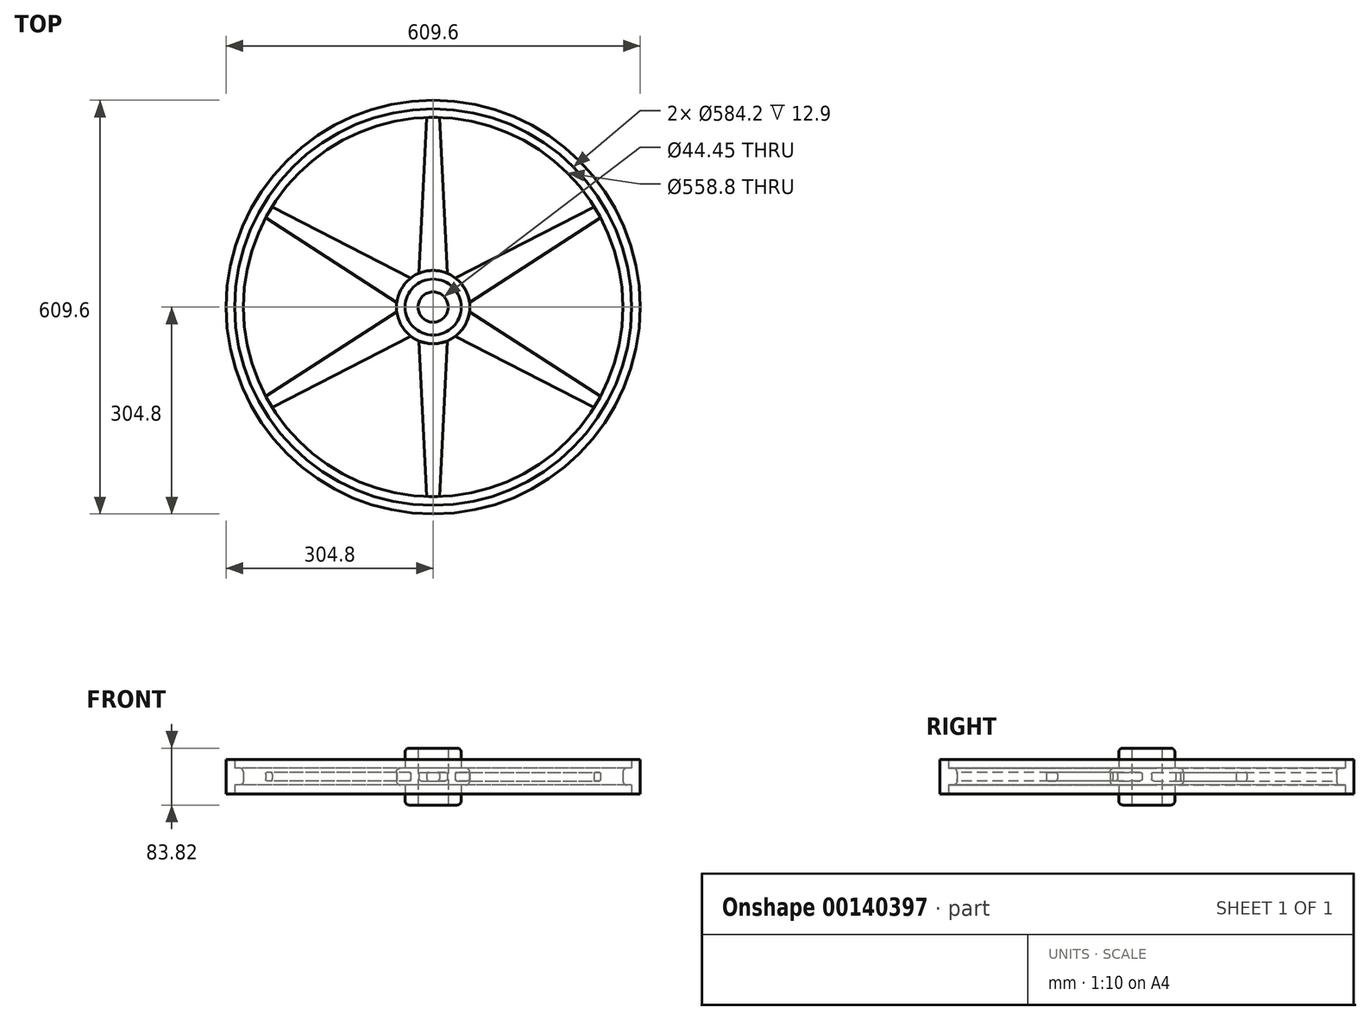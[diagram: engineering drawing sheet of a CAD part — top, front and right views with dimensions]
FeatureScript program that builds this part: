
annotation { "Feature Type Name" : "Feature", "Feature Type Description" : "" }
export const myFeature = defineFeature(function(context is Context, id is Id, definition is map)
    precondition{}
    {
        {
            var Q0;
            Q0=qCreatedBy(makeId("Top.planeOp"),FACE);
            var sketch = newSketch(context, id + "F0", { "sketchPlane" : qUnion([Q0])});
            skCircle(sketch, "E0", {"center": v(0, 0) * mm, "radius": 22.23 * mm});
            skCircle(sketch, "E1.0", {"center": v(0, 0) * mm, "radius": 41.28 * mm});
            skCircle(sketch, "E2.0", {"center": v(0, 0) * mm, "radius": 53.98 * mm});
            skCircle(sketch, "E3", {"center": v(0, 0) * mm, "radius": 304.8 * mm});
            skCircle(sketch, "E4.0", {"center": v(0, 0) * mm, "radius": 292.1 * mm});
            skCircle(sketch, "E5.0", {"center": v(0, 0) * mm, "radius": 279.4 * mm});
            skLineSegment(sketch, "E6", {"start": v(-20.86, 49.78) * mm, "end": v(-9.37, 279.24) * mm});
            skLineSegment(sketch, "E7.MirrorCS", {"start": v(20.86, 49.78) * mm, "end": v(9.37, 279.24) * mm});
            skLineSegment(sketch, "E8.1.0", {"start": v(-53.54, 6.83) * mm, "end": v(-246.52, 131.5) * mm});
            skLineSegment(sketch, "E8.1.1", {"start": v(-32.69, 42.95) * mm, "end": v(-237.15, 147.74) * mm});
            skLineSegment(sketch, "E8.2.0", {"start": v(-32.69, -42.95) * mm, "end": v(-237.15, -147.74) * mm});
            skLineSegment(sketch, "E8.2.1", {"start": v(-53.54, -6.83) * mm, "end": v(-246.52, -131.5) * mm});
            skLineSegment(sketch, "E9.1.3.0", {"start": v(20.86, -49.78) * mm, "end": v(9.37, -279.24) * mm});
            skLineSegment(sketch, "E9.3.3.0", {"start": v(-20.86, -49.78) * mm, "end": v(-9.37, -279.24) * mm});
            skLineSegment(sketch, "E9.1.4.0", {"start": v(53.54, -6.83) * mm, "end": v(246.52, -131.5) * mm});
            skLineSegment(sketch, "E9.3.4.0", {"start": v(32.69, -42.95) * mm, "end": v(237.15, -147.74) * mm});
            skLineSegment(sketch, "E9.1.5.0", {"start": v(32.69, 42.95) * mm, "end": v(237.15, 147.74) * mm});
            skLineSegment(sketch, "E9.3.5.0", {"start": v(53.54, 6.83) * mm, "end": v(246.52, 131.5) * mm});
            skSolve(sketch);
        }
        {
            var Q0;
            Q0=makeQuery(id+"F0.imprint","IMPRINT",FACE,{"disambiguationData":[TD([[makeQuery(id+"F0.imprint","IMPRINT",EDGE,{"derivedFrom":sQuery(id+"F0.wireOp",EDGE,"E4.0")}),1.0]])]});
            var Q1;
            Q1=makeQuery(id+"F0.imprint","IMPRINT",FACE,{"disambiguationData":[TD([[makeQuery(id+"F0.imprint","IMPRINT",EDGE,{"derivedFrom":sQuery(id+"F0.wireOp",EDGE,"E1.0")}),-1.0]])]});
            extrude(context, id + "F1", {"entities" : qUnion([Q0, Q1]), "endBound" : BoundingType.SYMMETRIC, "depth" : 25 * mm});
        }
        {
            var Q0;
            Q0=makeQuery(id+"F0.imprint","IMPRINT",FACE,{"disambiguationData":[TD([[makeQuery(id+"F0.imprint","IMPRINT",EDGE,{"derivedFrom":sQuery(id+"F0.wireOp",EDGE,"E3")}),1.0]])]});
            extrude(context, id + "F2", {"entities" : qUnion([Q0]), "operationType" : NewBodyOperationType.ADD, "endBound" : BoundingType.SYMMETRIC, "depth" : 50.8 * mm});
        }
        {
            var Q0;
            {var subQ0=sQuery(id+"F0.wireOp",EDGE,"E8.2.0");Q0=makeQuery(id+"F0.imprint","IMPRINT",FACE,{"disambiguationData":[TD([[makeQuery(id+"F0.imprint","IMPRINT",EDGE,{"derivedFrom":subQ0}),-1.0]])]});}
            var Q1;
            {var subQ0=sQuery(id+"F0.wireOp",EDGE,"E8.1.0");Q1=makeQuery(id+"F0.imprint","IMPRINT",FACE,{"disambiguationData":[TD([[makeQuery(id+"F0.imprint","IMPRINT",EDGE,{"derivedFrom":subQ0}),-1.0]])]});}
            var Q2;
            {var subQ0=sQuery(id+"F0.wireOp",EDGE,"E6");Q2=makeQuery(id+"F0.imprint","IMPRINT",FACE,{"disambiguationData":[TD([[makeQuery(id+"F0.imprint","IMPRINT",EDGE,{"derivedFrom":subQ0}),-1.0]])]});}
            var Q3;
            {var subQ0=sQuery(id+"F0.wireOp",EDGE,"E9.1.5.0");Q3=makeQuery(id+"F0.imprint","IMPRINT",FACE,{"disambiguationData":[TD([[makeQuery(id+"F0.imprint","IMPRINT",EDGE,{"derivedFrom":subQ0}),-1.0]])]});}
            var Q4;
            {var subQ0=sQuery(id+"F0.wireOp",EDGE,"E9.1.4.0");Q4=makeQuery(id+"F0.imprint","IMPRINT",FACE,{"disambiguationData":[TD([[makeQuery(id+"F0.imprint","IMPRINT",EDGE,{"derivedFrom":subQ0}),-1.0]])]});}
            var Q5;
            {var subQ0=sQuery(id+"F0.wireOp",EDGE,"E9.1.3.0");Q5=makeQuery(id+"F0.imprint","IMPRINT",FACE,{"disambiguationData":[TD([[makeQuery(id+"F0.imprint","IMPRINT",EDGE,{"derivedFrom":subQ0}),-1.0]])]});}
            extrude(context, id + "F3", {"entities" : qUnion([Q0, Q1, Q2, Q3, Q4, Q5]), "endBound" : BoundingType.SYMMETRIC, "depth" : 12.7 * mm});
        }
        {
            var Q0;
            Q0=makeQuery(id+"F0.imprint","IMPRINT",FACE,{"disambiguationData":[TD([[makeQuery(id+"F0.imprint","IMPRINT",EDGE,{"derivedFrom":sQuery(id+"F0.wireOp",EDGE,"E0")}),-1.0]])]});
            extrude(context, id + "F4", {"entities" : qUnion([Q0]), "operationType" : NewBodyOperationType.ADD, "endBound" : BoundingType.SYMMETRIC, "depth" : 83.82 * mm});
        }
        {
            var Q0;
            Q0=makeQuery(id+"F4.opExtrude","CAP_EDGE",EDGE,{"disambiguationData":[OSD([sQuery(id+"F0.wireOp",EDGE,"E1.0")])],"isStart":false});
            var Q1;
            Q1=makeQuery(id+"F4.opExtrude","CAP_EDGE",EDGE,{"disambiguationData":[OSD([sQuery(id+"F0.wireOp",EDGE,"E1.0")])],"isStart":true});
            var Q2;
            Q2=makeQuery(id+"F1.opExtrude","CAP_EDGE",EDGE,{"disambiguationData":[OSD([sQuery(id+"F0.wireOp",EDGE,"E2.0")])],"isStart":false});
            var Q3;
            Q3=makeQuery(id+"F1.opExtrude","CAP_EDGE",EDGE,{"disambiguationData":[OSD([sQuery(id+"F0.wireOp",EDGE,"E2.0")])],"isStart":true});
            var Q4;
            Q4=makeQuery(id+"F1.opExtrude","CAP_EDGE",EDGE,{"disambiguationData":[OSD([sQuery(id+"F0.wireOp",EDGE,"E5.0")])],"isStart":false});
            var Q5;
            Q5=makeQuery(id+"F1.opExtrude","CAP_EDGE",EDGE,{"disambiguationData":[OSD([sQuery(id+"F0.wireOp",EDGE,"E5.0")])],"isStart":true});
            fillet(context, id + "F5", {"entities" : qUnion([Q0, Q1, Q2, Q3, Q4, Q5]), "radius" : 6 * mm, "tangentPropagation" : true, "allowEdgeOverflow" : false});
        }
        {
            var Q0;
            Q0=makeQuery(id+"F3.opExtrude","CAP_EDGE",EDGE,{"disambiguationData":[OSD([sQuery(id+"F0.wireOp",EDGE,"E9.1.4.0")])],"isStart":false});
            var Q1;
            Q1=makeQuery(id+"F3.opExtrude","CAP_EDGE",EDGE,{"disambiguationData":[OSD([sQuery(id+"F0.wireOp",EDGE,"E9.1.4.0")])],"isStart":true});
            var Q2;
            Q2=makeQuery(id+"F3.opExtrude","CAP_EDGE",EDGE,{"disambiguationData":[OSD([sQuery(id+"F0.wireOp",EDGE,"E9.3.4.0")])],"isStart":false});
            var Q3;
            Q3=makeQuery(id+"F3.opExtrude","CAP_EDGE",EDGE,{"disambiguationData":[OSD([sQuery(id+"F0.wireOp",EDGE,"E9.3.5.0")])],"isStart":false});
            var Q4;
            Q4=makeQuery(id+"F3.opExtrude","CAP_EDGE",EDGE,{"disambiguationData":[OSD([sQuery(id+"F0.wireOp",EDGE,"E9.1.5.0")])],"isStart":false});
            var Q5;
            Q5=makeQuery(id+"F3.opExtrude","CAP_EDGE",EDGE,{"disambiguationData":[OSD([sQuery(id+"F0.wireOp",EDGE,"E9.1.5.0")])],"isStart":true});
            var Q6;
            Q6=makeQuery(id+"F3.opExtrude","CAP_EDGE",EDGE,{"disambiguationData":[OSD([sQuery(id+"F0.wireOp",EDGE,"E7.MirrorCS")])],"isStart":false});
            var Q7;
            Q7=makeQuery(id+"F3.opExtrude","CAP_EDGE",EDGE,{"disambiguationData":[OSD([sQuery(id+"F0.wireOp",EDGE,"E6")])],"isStart":false});
            var Q8;
            Q8=makeQuery(id+"F3.opExtrude","CAP_EDGE",EDGE,{"disambiguationData":[OSD([sQuery(id+"F0.wireOp",EDGE,"E6")])],"isStart":true});
            var Q9;
            Q9=makeQuery(id+"F3.opExtrude","CAP_EDGE",EDGE,{"disambiguationData":[OSD([sQuery(id+"F0.wireOp",EDGE,"E8.1.1")])],"isStart":true});
            var Q10;
            Q10=makeQuery(id+"F3.opExtrude","CAP_EDGE",EDGE,{"disambiguationData":[OSD([sQuery(id+"F0.wireOp",EDGE,"E8.1.1")])],"isStart":false});
            var Q11;
            Q11=makeQuery(id+"F3.opExtrude","CAP_EDGE",EDGE,{"disambiguationData":[OSD([sQuery(id+"F0.wireOp",EDGE,"E8.1.0")])],"isStart":false});
            var Q12;
            Q12=makeQuery(id+"F3.opExtrude","CAP_EDGE",EDGE,{"disambiguationData":[OSD([sQuery(id+"F0.wireOp",EDGE,"E8.2.1")])],"isStart":true});
            var Q13;
            Q13=makeQuery(id+"F3.opExtrude","CAP_EDGE",EDGE,{"disambiguationData":[OSD([sQuery(id+"F0.wireOp",EDGE,"E8.2.1")])],"isStart":false});
            var Q14;
            Q14=makeQuery(id+"F3.opExtrude","CAP_EDGE",EDGE,{"disambiguationData":[OSD([sQuery(id+"F0.wireOp",EDGE,"E8.2.0")])],"isStart":false});
            var Q15;
            Q15=makeQuery(id+"F3.opExtrude","CAP_EDGE",EDGE,{"disambiguationData":[OSD([sQuery(id+"F0.wireOp",EDGE,"E9.3.3.0")])],"isStart":true});
            var Q16;
            Q16=makeQuery(id+"F3.opExtrude","CAP_EDGE",EDGE,{"disambiguationData":[OSD([sQuery(id+"F0.wireOp",EDGE,"E9.3.3.0")])],"isStart":false});
            var Q17;
            Q17=makeQuery(id+"F3.opExtrude","CAP_EDGE",EDGE,{"disambiguationData":[OSD([sQuery(id+"F0.wireOp",EDGE,"E9.1.3.0")])],"isStart":false});
            var Q18;
            Q18=makeQuery(id+"F3.opExtrude","CAP_EDGE",EDGE,{"disambiguationData":[OSD([sQuery(id+"F0.wireOp",EDGE,"E9.1.3.0")])],"isStart":true});
            var Q19;
            Q19=makeQuery(id+"F3.opExtrude","CAP_EDGE",EDGE,{"disambiguationData":[OSD([sQuery(id+"F0.wireOp",EDGE,"E8.2.0")])],"isStart":true});
            var Q20;
            Q20=makeQuery(id+"F3.opExtrude","CAP_EDGE",EDGE,{"disambiguationData":[OSD([sQuery(id+"F0.wireOp",EDGE,"E8.1.0")])],"isStart":true});
            var Q21;
            Q21=makeQuery(id+"F3.opExtrude","CAP_EDGE",EDGE,{"disambiguationData":[OSD([sQuery(id+"F0.wireOp",EDGE,"E9.3.5.0")])],"isStart":true});
            var Q22;
            Q22=makeQuery(id+"F3.opExtrude","CAP_EDGE",EDGE,{"disambiguationData":[OSD([sQuery(id+"F0.wireOp",EDGE,"E9.3.4.0")])],"isStart":true});
            var Q23;
            Q23=makeQuery(id+"F3.opExtrude","CAP_EDGE",EDGE,{"disambiguationData":[OSD([sQuery(id+"F0.wireOp",EDGE,"E7.MirrorCS")])],"isStart":true});
            fillet(context, id + "F6", {"entities" : qUnion([Q0, Q1, Q2, Q3, Q4, Q5, Q6, Q7, Q8, Q9, Q10, Q11, Q12, Q13, Q14, Q15, Q16, Q17, Q18, Q19, Q20, Q21, Q22, Q23]), "radius" : 3 * mm, "tangentPropagation" : true, "allowEdgeOverflow" : false});
        }
    });
